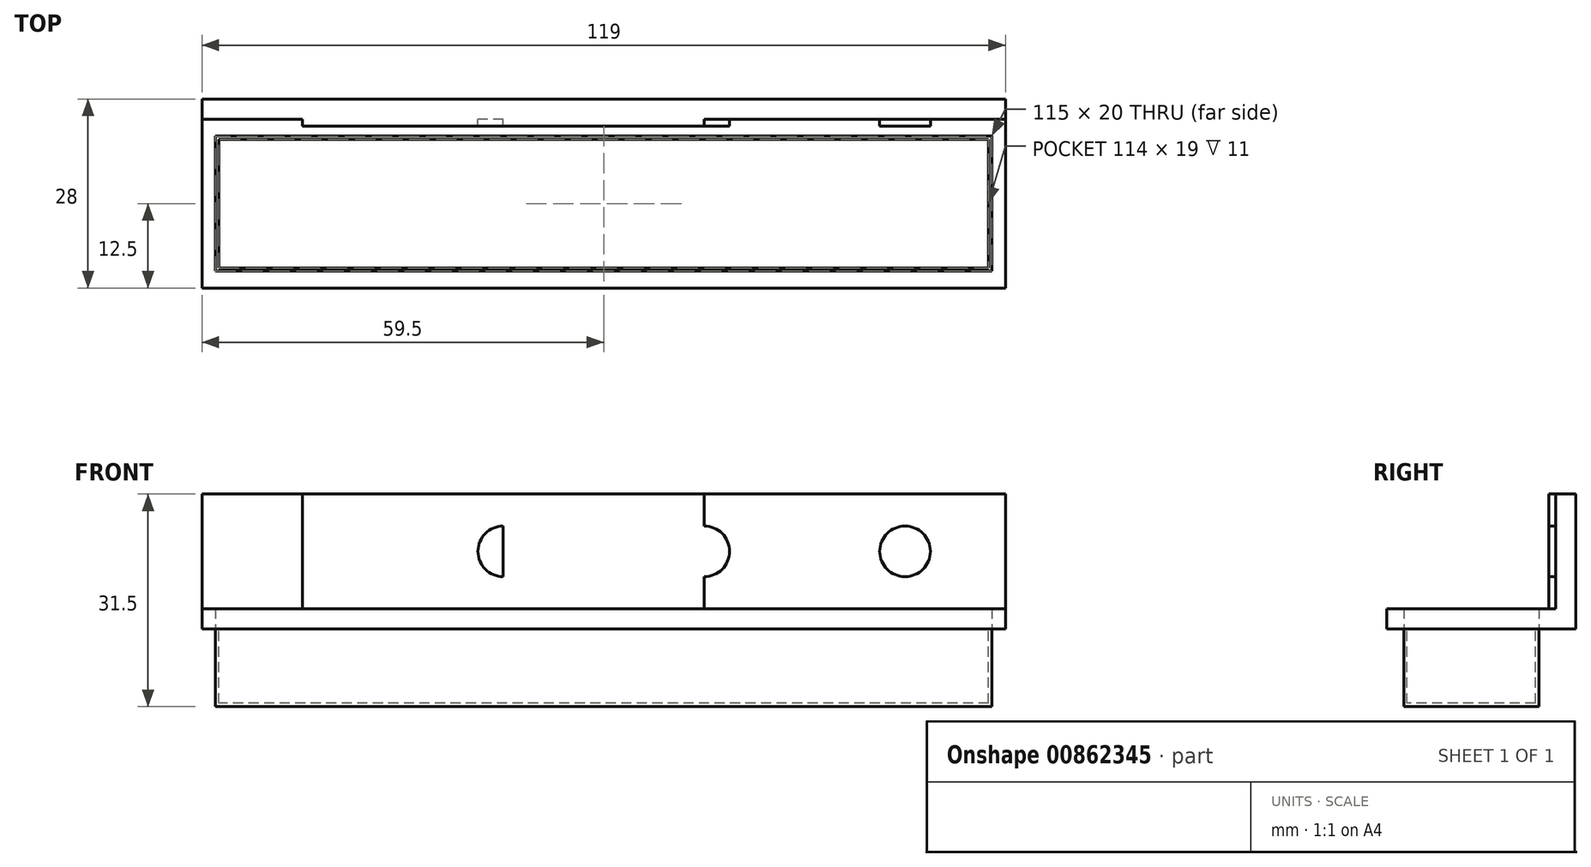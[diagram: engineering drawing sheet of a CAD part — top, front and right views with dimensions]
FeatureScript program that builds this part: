
annotation { "Feature Type Name" : "Feature", "Feature Type Description" : "" }
export const myFeature = defineFeature(function(context is Context, id is Id, definition is map)
    precondition{}
    {
        {
            var Q0;
            Q0=qCreatedBy(makeId("Top.planeOp"),FACE);
            var sketch = newSketch(context, id + "F0", { "sketchPlane" : qUnion([Q0])});
            skLineSegment(sketch, "E0.bottom", {"start": v(57.5, 10) * mm, "end": v(-57.5, 10) * mm});
            skLineSegment(sketch, "E0.top", {"start": v(57.5, -10) * mm, "end": v(-57.5, -10) * mm});
            skLineSegment(sketch, "E0.left", {"start": v(57.5, 10) * mm, "end": v(57.5, -10) * mm});
            skLineSegment(sketch, "E0.right", {"start": v(-57.5, 10) * mm, "end": v(-57.5, -10) * mm});
            skPoint(sketch, "E0.middle", {"position": v(0, 0) * mm});
            skSolve(sketch);
        }
        {
            var Q0;
            Q0=makeQuery(id+"F0.imprint","IMPRINT",FACE,{"disambiguationData":[TD([[makeQuery(id+"F0.imprint","IMPRINT",EDGE,{"derivedFrom":sQuery(id+"F0.wireOp",EDGE,"E0.bottom")}),1.0]])]});
            extrude(context, id + "F1", {"entities" : qUnion([Q0]), "depth" : 11.5 * mm, "offsetDistance" : 25 * mm});
        }
        {
            var Q0;
            Q0=makeQuery(id+"F1.opExtrude","CAP_FACE",FACE,{"disambiguationData":[OSD([sQuery(id+"F0.wireOp",EDGE,"E0.bottom"),sQuery(id+"F0.wireOp",EDGE,"E0.top"),sQuery(id+"F0.wireOp",EDGE,"E0.left"),sQuery(id+"F0.wireOp",EDGE,"E0.right")])],"isStart":false});
            var sketch = newSketch(context, id + "F2", { "sketchPlane" : qUnion([Q0])});
            skLineSegment(sketch, "E1.bottom", {"start": v(59.5, 12.5) * mm, "end": v(-59.5, 12.5) * mm});
            skLineSegment(sketch, "E1.top", {"start": v(59.5, -12.5) * mm, "end": v(-59.5, -12.5) * mm});
            skLineSegment(sketch, "E1.left", {"start": v(59.5, 12.5) * mm, "end": v(59.5, -12.5) * mm});
            skLineSegment(sketch, "E1.right", {"start": v(-59.5, 12.5) * mm, "end": v(-59.5, -12.5) * mm});
            skPoint(sketch, "E1.middle", {"position": v(0, 0) * mm});
            skSolve(sketch);
        }
        {
            var Q0;
            Q0=makeQuery(id+"F2.imprint","IMPRINT",FACE,{"disambiguationData":[TD([[makeQuery(id+"F2.imprint","IMPRINT",EDGE,{"derivedFrom":sQuery(id+"F2.wireOp",EDGE,"E1.bottom")}),1.0]])]});
            extrude(context, id + "F3", {"entities" : qUnion([Q0]), "depth" : 3 * mm, "offsetDistance" : 25 * mm});
        }
        {
            var Q0;
            Q0=makeQuery(id+"F1.opExtrude","CAP_FACE",FACE,{"disambiguationData":[OSD([sQuery(id+"F0.wireOp",EDGE,"E0.bottom"),sQuery(id+"F0.wireOp",EDGE,"E0.top"),sQuery(id+"F0.wireOp",EDGE,"E0.left"),sQuery(id+"F0.wireOp",EDGE,"E0.right")])],"isStart":false});
            var sketch = newSketch(context, id + "F4", { "sketchPlane" : qUnion([Q0])});
            skLineSegment(sketch, "E2.bottom", {"start": v(57, 9.5) * mm, "end": v(-57, 9.5) * mm});
            skLineSegment(sketch, "E2.top", {"start": v(57, -9.5) * mm, "end": v(-57, -9.5) * mm});
            skLineSegment(sketch, "E2.left", {"start": v(57, 9.5) * mm, "end": v(57, -9.5) * mm});
            skLineSegment(sketch, "E2.right", {"start": v(-57, 9.5) * mm, "end": v(-57, -9.5) * mm});
            skPoint(sketch, "E2.middle", {"position": v(0, 0) * mm});
            skSolve(sketch);
        }
        {
            var Q0;
            Q0=makeQuery(id+"F4.imprint","IMPRINT",FACE,{"disambiguationData":[TD([[makeQuery(id+"F4.imprint","IMPRINT",EDGE,{"derivedFrom":sQuery(id+"F4.wireOp",EDGE,"E2.bottom")}),1.0]])]});
            extrude(context, id + "F5", {"entities" : qUnion([Q0]), "operationType" : NewBodyOperationType.REMOVE, "oppositeDirection" : true, "depth" : 11 * mm, "offsetDistance" : 25 * mm});
        }
        {
            var Q0;
            Q0=makeQuery(id+"F3.opExtrude","SWEPT_FACE",FACE,{"disambiguationData":[OSD([sQuery(id+"F2.wireOp",EDGE,"E1.bottom")])]});
            var sketch = newSketch(context, id + "F6", { "sketchPlane" : qUnion([Q0])});
            skLineSegment(sketch, "E3.bottom", {"start": v(-59.5, 11.5) * mm, "end": v(59.5, 11.5) * mm});
            skLineSegment(sketch, "E3.top", {"start": v(-59.5, 31.5) * mm, "end": v(59.5, 31.5) * mm});
            skLineSegment(sketch, "E3.left", {"start": v(-59.5, 11.5) * mm, "end": v(-59.5, 31.5) * mm});
            skLineSegment(sketch, "E3.right", {"start": v(59.5, 11.5) * mm, "end": v(59.5, 31.5) * mm});
            skSolve(sketch);
        }
        {
            var Q0;
            {var subQ0=sQuery(id+"F6.wireOp",EDGE,"E3.top");Q0=makeQuery(id+"F6.imprint","IMPRINT",FACE,{"disambiguationData":[TD([[makeQuery(id+"F6.imprint","IMPRINT",EDGE,{"derivedFrom":subQ0}),-1.0]])]});}
            var Q1;
            {var subQ0=sQuery(id+"F6.wireOp",EDGE,"E3.bottom");Q1=makeQuery(id+"F6.imprint","IMPRINT",FACE,{"disambiguationData":[TD([[makeQuery(id+"F6.imprint","IMPRINT",EDGE,{"derivedFrom":subQ0}),1.0]])]});}
            extrude(context, id + "F7", {"entities" : qUnion([Q0, Q1]), "operationType" : NewBodyOperationType.ADD, "depth" : 3 * mm, "offsetDistance" : 25 * mm});
        }
        {
            var Q0;
            Q0=makeQuery(id+"F7.opExtrude","CAP_FACE",FACE,{"disambiguationData":[OSD([sQuery(id+"F6.wireOp",EDGE,"E3.bottom"),sQuery(id+"F6.wireOp",EDGE,"E3.top"),sQuery(id+"F6.wireOp",EDGE,"E3.left"),sQuery(id+"F6.wireOp",EDGE,"E3.right")])],"isStart":true});
            var sketch = newSketch(context, id + "F8", { "sketchPlane" : qUnion([Q0])});
            skLineSegment(sketch, "E4", {"start": v(-59.5, 23) * mm, "end": v(59.5, 23) * mm});
            skLineSegment(sketch, "E5", {"start": v(-44.62, 31.5) * mm, "end": v(-44.62, 14.5) * mm});
            skLineSegment(sketch, "E6", {"start": v(-14.87, 31.5) * mm, "end": v(-14.87, 14.5) * mm});
            skLineSegment(sketch, "E7", {"start": v(14.88, 31.5) * mm, "end": v(14.88, 14.5) * mm});
            skLineSegment(sketch, "E8", {"start": v(44.63, 31.5) * mm, "end": v(44.63, 14.5) * mm});
            skCircle(sketch, "E9", {"center": v(-44.62, 23) * mm, "radius": 3.75 * mm});
            skCircle(sketch, "E10", {"center": v(-14.87, 23) * mm, "radius": 3.75 * mm});
            skCircle(sketch, "E11", {"center": v(14.88, 23) * mm, "radius": 3.75 * mm});
            skCircle(sketch, "E12", {"center": v(44.63, 23) * mm, "radius": 3.75 * mm});
            skSolve(sketch);
        }
        {
            var Q0;
            {var subQ0=sQuery(id+"F8.wireOp",EDGE,"E9");var subQ1=sQuery(id+"F8.wireOp",EDGE,"E4");var subQ2=makeQuery(id+"F8.imprint","INTERSECT",VERTEX,{"disambiguationData":[OD(0.0)],"derivedFrom":[subQ1,subQ0]});Q0=makeQuery(id+"F8.imprint","IMPRINT",FACE,{"disambiguationData":[TD([[makeQuery(id+"F8.imprint","IMPRINT",EDGE,{"disambiguationData":[TD([[subQ2,-1.0]])],"derivedFrom":subQ1}),-1.0]])]});}
            var Q1;
            {var subQ0=sQuery(id+"F8.wireOp",EDGE,"E5");var subQ1=sQuery(id+"F8.wireOp",EDGE,"E4");var subQ2=makeQuery(id+"F8.imprint","INTERSECT",VERTEX,{"derivedFrom":[subQ1,subQ0]});Q1=makeQuery(id+"F8.imprint","IMPRINT",FACE,{"disambiguationData":[TD([[makeQuery(id+"F8.imprint","IMPRINT",EDGE,{"disambiguationData":[TD([[subQ2,-1.0]])],"derivedFrom":subQ1}),-1.0]])]});}
            var Q2;
            {var subQ0=sQuery(id+"F8.wireOp",EDGE,"E5");var subQ1=sQuery(id+"F8.wireOp",EDGE,"E4");var subQ2=makeQuery(id+"F8.imprint","INTERSECT",VERTEX,{"derivedFrom":[subQ1,subQ0]});Q2=makeQuery(id+"F8.imprint","IMPRINT",FACE,{"disambiguationData":[TD([[makeQuery(id+"F8.imprint","IMPRINT",EDGE,{"disambiguationData":[TD([[subQ2,-1.0]])],"derivedFrom":subQ1}),1.0]])]});}
            var Q3;
            {var subQ0=sQuery(id+"F8.wireOp",EDGE,"E9");var subQ1=sQuery(id+"F8.wireOp",EDGE,"E4");var subQ2=makeQuery(id+"F8.imprint","INTERSECT",VERTEX,{"disambiguationData":[OD(0.0)],"derivedFrom":[subQ1,subQ0]});Q3=makeQuery(id+"F8.imprint","IMPRINT",FACE,{"disambiguationData":[TD([[makeQuery(id+"F8.imprint","IMPRINT",EDGE,{"disambiguationData":[TD([[subQ2,-1.0]])],"derivedFrom":subQ1}),1.0]])]});}
            var Q4;
            {var subQ0=sQuery(id+"F8.wireOp",EDGE,"E10");var subQ1=sQuery(id+"F8.wireOp",EDGE,"E4");var subQ2=makeQuery(id+"F8.imprint","INTERSECT",VERTEX,{"disambiguationData":[OD(0.0)],"derivedFrom":[subQ1,subQ0]});Q4=makeQuery(id+"F8.imprint","IMPRINT",FACE,{"disambiguationData":[TD([[makeQuery(id+"F8.imprint","IMPRINT",EDGE,{"disambiguationData":[TD([[subQ2,-1.0]])],"derivedFrom":subQ1}),1.0]])]});}
            var Q5;
            {var subQ0=sQuery(id+"F8.wireOp",EDGE,"E6");var subQ1=sQuery(id+"F8.wireOp",EDGE,"E4");var subQ2=makeQuery(id+"F8.imprint","INTERSECT",VERTEX,{"derivedFrom":[subQ1,subQ0]});Q5=makeQuery(id+"F8.imprint","IMPRINT",FACE,{"disambiguationData":[TD([[makeQuery(id+"F8.imprint","IMPRINT",EDGE,{"disambiguationData":[TD([[subQ2,-1.0]])],"derivedFrom":subQ1}),1.0]])]});}
            var Q6;
            {var subQ0=sQuery(id+"F8.wireOp",EDGE,"E10");var subQ1=sQuery(id+"F8.wireOp",EDGE,"E4");var subQ2=makeQuery(id+"F8.imprint","INTERSECT",VERTEX,{"disambiguationData":[OD(0.0)],"derivedFrom":[subQ1,subQ0]});Q6=makeQuery(id+"F8.imprint","IMPRINT",FACE,{"disambiguationData":[TD([[makeQuery(id+"F8.imprint","IMPRINT",EDGE,{"disambiguationData":[TD([[subQ2,-1.0]])],"derivedFrom":subQ1}),-1.0]])]});}
            var Q7;
            {var subQ0=sQuery(id+"F8.wireOp",EDGE,"E6");var subQ1=sQuery(id+"F8.wireOp",EDGE,"E4");var subQ2=makeQuery(id+"F8.imprint","INTERSECT",VERTEX,{"derivedFrom":[subQ1,subQ0]});Q7=makeQuery(id+"F8.imprint","IMPRINT",FACE,{"disambiguationData":[TD([[makeQuery(id+"F8.imprint","IMPRINT",EDGE,{"disambiguationData":[TD([[subQ2,-1.0]])],"derivedFrom":subQ1}),-1.0]])]});}
            var Q8;
            {var subQ0=sQuery(id+"F8.wireOp",EDGE,"E7");var subQ1=sQuery(id+"F8.wireOp",EDGE,"E4");var subQ2=makeQuery(id+"F8.imprint","INTERSECT",VERTEX,{"derivedFrom":[subQ1,subQ0]});Q8=makeQuery(id+"F8.imprint","IMPRINT",FACE,{"disambiguationData":[TD([[makeQuery(id+"F8.imprint","IMPRINT",EDGE,{"disambiguationData":[TD([[subQ2,-1.0]])],"derivedFrom":subQ1}),1.0]])]});}
            var Q9;
            {var subQ0=sQuery(id+"F8.wireOp",EDGE,"E11");var subQ1=sQuery(id+"F8.wireOp",EDGE,"E4");var subQ2=makeQuery(id+"F8.imprint","INTERSECT",VERTEX,{"disambiguationData":[OD(0.0)],"derivedFrom":[subQ1,subQ0]});Q9=makeQuery(id+"F8.imprint","IMPRINT",FACE,{"disambiguationData":[TD([[makeQuery(id+"F8.imprint","IMPRINT",EDGE,{"disambiguationData":[TD([[subQ2,-1.0]])],"derivedFrom":subQ1}),1.0]])]});}
            var Q10;
            {var subQ0=sQuery(id+"F8.wireOp",EDGE,"E11");var subQ1=sQuery(id+"F8.wireOp",EDGE,"E4");var subQ2=makeQuery(id+"F8.imprint","INTERSECT",VERTEX,{"disambiguationData":[OD(0.0)],"derivedFrom":[subQ1,subQ0]});Q10=makeQuery(id+"F8.imprint","IMPRINT",FACE,{"disambiguationData":[TD([[makeQuery(id+"F8.imprint","IMPRINT",EDGE,{"disambiguationData":[TD([[subQ2,-1.0]])],"derivedFrom":subQ1}),-1.0]])]});}
            var Q11;
            {var subQ0=sQuery(id+"F8.wireOp",EDGE,"E7");var subQ1=sQuery(id+"F8.wireOp",EDGE,"E4");var subQ2=makeQuery(id+"F8.imprint","INTERSECT",VERTEX,{"derivedFrom":[subQ1,subQ0]});Q11=makeQuery(id+"F8.imprint","IMPRINT",FACE,{"disambiguationData":[TD([[makeQuery(id+"F8.imprint","IMPRINT",EDGE,{"disambiguationData":[TD([[subQ2,-1.0]])],"derivedFrom":subQ1}),-1.0]])]});}
            var Q12;
            {var subQ0=sQuery(id+"F8.wireOp",EDGE,"E8");var subQ1=sQuery(id+"F8.wireOp",EDGE,"E4");var subQ2=makeQuery(id+"F8.imprint","INTERSECT",VERTEX,{"derivedFrom":[subQ1,subQ0]});Q12=makeQuery(id+"F8.imprint","IMPRINT",FACE,{"disambiguationData":[TD([[makeQuery(id+"F8.imprint","IMPRINT",EDGE,{"disambiguationData":[TD([[subQ2,-1.0]])],"derivedFrom":subQ1}),1.0]])]});}
            var Q13;
            {var subQ0=sQuery(id+"F8.wireOp",EDGE,"E12");var subQ1=sQuery(id+"F8.wireOp",EDGE,"E4");var subQ2=makeQuery(id+"F8.imprint","INTERSECT",VERTEX,{"disambiguationData":[OD(0.0)],"derivedFrom":[subQ1,subQ0]});Q13=makeQuery(id+"F8.imprint","IMPRINT",FACE,{"disambiguationData":[TD([[makeQuery(id+"F8.imprint","IMPRINT",EDGE,{"disambiguationData":[TD([[subQ2,-1.0]])],"derivedFrom":subQ1}),1.0]])]});}
            var Q14;
            {var subQ0=sQuery(id+"F8.wireOp",EDGE,"E12");var subQ1=sQuery(id+"F8.wireOp",EDGE,"E4");var subQ2=makeQuery(id+"F8.imprint","INTERSECT",VERTEX,{"disambiguationData":[OD(0.0)],"derivedFrom":[subQ1,subQ0]});Q14=makeQuery(id+"F8.imprint","IMPRINT",FACE,{"disambiguationData":[TD([[makeQuery(id+"F8.imprint","IMPRINT",EDGE,{"disambiguationData":[TD([[subQ2,-1.0]])],"derivedFrom":subQ1}),-1.0]])]});}
            var Q15;
            {var subQ0=sQuery(id+"F8.wireOp",EDGE,"E8");var subQ1=sQuery(id+"F8.wireOp",EDGE,"E4");var subQ2=makeQuery(id+"F8.imprint","INTERSECT",VERTEX,{"derivedFrom":[subQ1,subQ0]});Q15=makeQuery(id+"F8.imprint","IMPRINT",FACE,{"disambiguationData":[TD([[makeQuery(id+"F8.imprint","IMPRINT",EDGE,{"disambiguationData":[TD([[subQ2,-1.0]])],"derivedFrom":subQ1}),-1.0]])]});}
            extrude(context, id + "F9", {"entities" : qUnion([Q0, Q1, Q2, Q3, Q4, Q5, Q6, Q7, Q8, Q9, Q10, Q11, Q12, Q13, Q14, Q15]), "operationType" : NewBodyOperationType.ADD, "depth" : 1 * mm, "offsetDistance" : 25 * mm});
        }
    });
